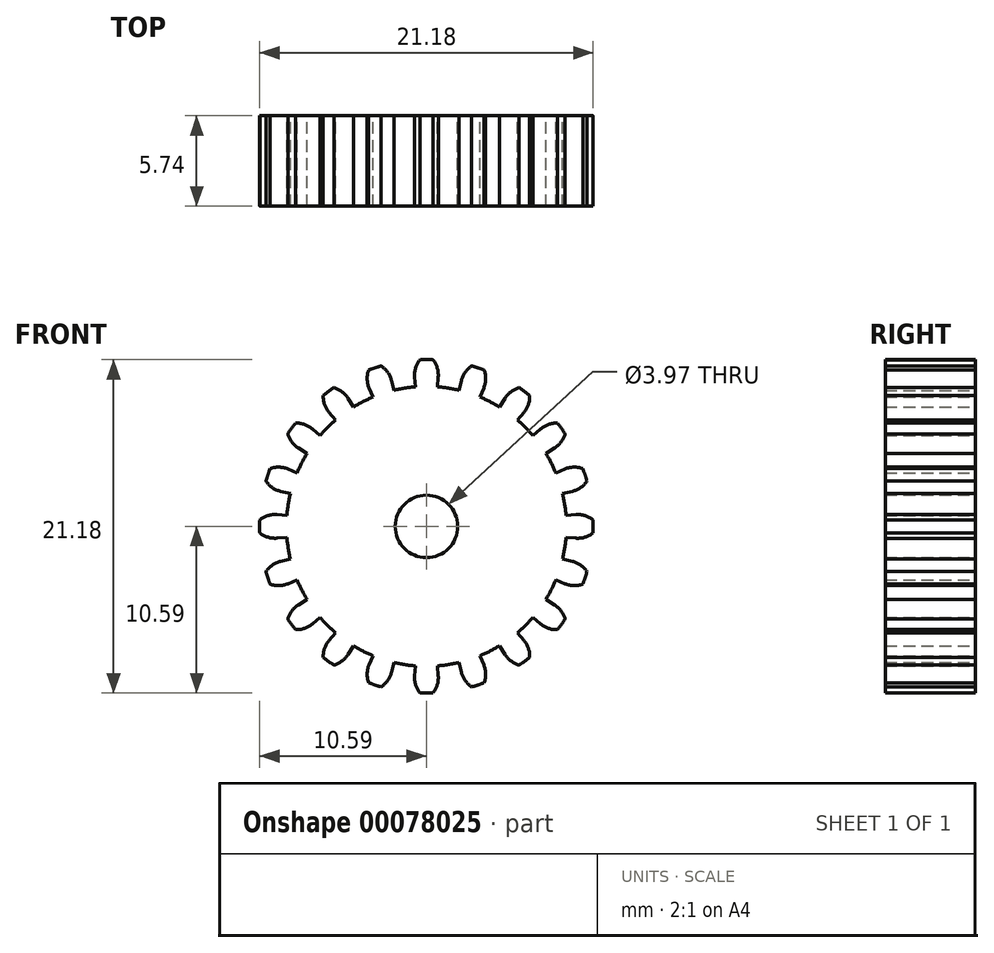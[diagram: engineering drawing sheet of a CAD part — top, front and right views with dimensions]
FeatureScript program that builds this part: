
annotation { "Feature Type Name" : "Feature", "Feature Type Description" : "" }
export const myFeature = defineFeature(function(context is Context, id is Id, definition is map)
    precondition{}
    {
        {
            var Q0;
            Q0=qCreatedBy(makeId("Front.planeOp"),FACE);
            var sketch = newSketch(context, id + "F0", { "sketchPlane" : qUnion([Q0])});
            skCircle(sketch, "E0", {"center": v(0, 0) * mm, "radius": 10.6 * mm, "construction": true});
            skCircle(sketch, "E1", {"center": v(0, 0) * mm, "radius": 9.53 * mm, "construction": true});
            skCircle(sketch, "E2", {"center": v(0, 0) * mm, "radius": 8.9 * mm, "construction": true});
            skLineSegment(sketch, "E3", {"start": v(0, 0) * mm, "end": v(8.78, 1.4) * mm, "construction": true});
            skLineSegment(sketch, "E4", {"start": v(0, 0) * mm, "end": v(6.61, 0) * mm, "construction": true});
            skLineSegment(sketch, "E5", {"start": v(0, 0) * mm, "end": v(6.84, 0.54) * mm, "construction": true});
            skLineSegment(sketch, "E6", {"start": v(0, 0) * mm, "end": v(7.15, 0.28) * mm, "construction": true});
            skArc(sketch, "E7", {"start": v(10.58, 0.42) * mm, "mid": v(10.59, 0.2) * mm, "end": v(10.6, 0) * mm});
            skArc(sketch, "E8", {"start": v(8.78, 1.4) * mm, "mid": v(8.83, 1.04) * mm, "end": v(8.86, 0.7) * mm});
            skLineSegment(sketch, "E9", {"start": v(8.86, 0.7) * mm, "end": v(9.5, 0.75) * mm});
            skArc(sketch, "E10", {"start": v(9.5, 0.75) * mm, "mid": v(10.07, 0.68) * mm, "end": v(10.58, 0.42) * mm});
            skLineSegment(sketch, "E11", {"start": v(0, 0) * mm, "end": v(8.78, 1.4) * mm});
            skLineSegment(sketch, "E12", {"start": v(0, 0) * mm, "end": v(10.6, 0) * mm});
            skArc(sketch, "E13.MirrorCS", {"start": v(8.78, -1.4) * mm, "mid": v(8.83, -1.04) * mm, "end": v(8.86, -0.7) * mm});
            skLineSegment(sketch, "E14.MirrorCS", {"start": v(8.86, -0.7) * mm, "end": v(9.5, -0.75) * mm});
            skArc(sketch, "E15.MirrorCS", {"start": v(9.5, -0.75) * mm, "mid": v(10.07, -0.68) * mm, "end": v(10.58, -0.42) * mm});
            skArc(sketch, "E16.MirrorCS", {"start": v(10.58, -0.42) * mm, "mid": v(10.59, -0.2) * mm, "end": v(10.6, 0) * mm});
            skArc(sketch, "E17.1.0", {"start": v(7.92, 4.04) * mm, "mid": v(8.07, 3.72) * mm, "end": v(8.21, 3.4) * mm});
            skLineSegment(sketch, "E17.1.1", {"start": v(8.21, 3.4) * mm, "end": v(8.8, 3.65) * mm});
            skArc(sketch, "E17.1.2", {"start": v(8.8, 3.65) * mm, "mid": v(9.37, 3.76) * mm, "end": v(9.94, 3.67) * mm});
            skArc(sketch, "E17.1.3", {"start": v(9.94, 3.67) * mm, "mid": v(10, 3.47) * mm, "end": v(10.07, 3.27) * mm});
            skArc(sketch, "E17.1.4", {"start": v(10.2, 2.88) * mm, "mid": v(10.14, 3.07) * mm, "end": v(10.07, 3.27) * mm});
            skArc(sketch, "E17.1.5", {"start": v(9.26, 2.22) * mm, "mid": v(9.79, 2.46) * mm, "end": v(10.2, 2.88) * mm});
            skLineSegment(sketch, "E17.1.6", {"start": v(8.64, 2.08) * mm, "end": v(9.26, 2.22) * mm});
            skArc(sketch, "E17.1.7", {"start": v(8.78, 1.4) * mm, "mid": v(8.72, 1.73) * mm, "end": v(8.64, 2.08) * mm});
            skArc(sketch, "E17.2.0", {"start": v(6.29, 6.29) * mm, "mid": v(6.53, 6.03) * mm, "end": v(6.76, 5.77) * mm});
            skLineSegment(sketch, "E17.2.1", {"start": v(6.76, 5.77) * mm, "end": v(7.24, 6.19) * mm});
            skArc(sketch, "E17.2.2", {"start": v(7.24, 6.19) * mm, "mid": v(7.75, 6.47) * mm, "end": v(8.32, 6.56) * mm});
            skArc(sketch, "E17.2.3", {"start": v(8.32, 6.56) * mm, "mid": v(8.45, 6.4) * mm, "end": v(8.57, 6.23) * mm});
            skArc(sketch, "E17.2.4", {"start": v(8.8, 5.88) * mm, "mid": v(8.69, 6.06) * mm, "end": v(8.57, 6.23) * mm});
            skArc(sketch, "E17.2.5", {"start": v(8.12, 4.98) * mm, "mid": v(8.55, 5.37) * mm, "end": v(8.8, 5.88) * mm});
            skLineSegment(sketch, "E17.2.6", {"start": v(7.58, 4.65) * mm, "end": v(8.12, 4.98) * mm});
            skArc(sketch, "E17.2.7", {"start": v(7.92, 4.04) * mm, "mid": v(7.76, 4.34) * mm, "end": v(7.58, 4.65) * mm});
            skArc(sketch, "E17.3.0", {"start": v(4.04, 7.92) * mm, "mid": v(4.34, 7.76) * mm, "end": v(4.65, 7.58) * mm});
            skLineSegment(sketch, "E17.3.1", {"start": v(4.65, 7.58) * mm, "end": v(4.98, 8.12) * mm});
            skArc(sketch, "E17.3.2", {"start": v(4.98, 8.12) * mm, "mid": v(5.37, 8.55) * mm, "end": v(5.88, 8.8) * mm});
            skArc(sketch, "E17.3.3", {"start": v(5.88, 8.8) * mm, "mid": v(6.06, 8.69) * mm, "end": v(6.23, 8.57) * mm});
            skArc(sketch, "E17.3.4", {"start": v(6.56, 8.32) * mm, "mid": v(6.4, 8.45) * mm, "end": v(6.23, 8.57) * mm});
            skArc(sketch, "E17.3.5", {"start": v(6.19, 7.24) * mm, "mid": v(6.47, 7.75) * mm, "end": v(6.56, 8.32) * mm});
            skLineSegment(sketch, "E17.3.6", {"start": v(5.77, 6.76) * mm, "end": v(6.19, 7.24) * mm});
            skArc(sketch, "E17.3.7", {"start": v(6.29, 6.29) * mm, "mid": v(6.03, 6.53) * mm, "end": v(5.77, 6.76) * mm});
            skArc(sketch, "E17.4.0", {"start": v(1.4, 8.78) * mm, "mid": v(1.73, 8.72) * mm, "end": v(2.08, 8.64) * mm});
            skLineSegment(sketch, "E17.4.1", {"start": v(2.08, 8.64) * mm, "end": v(2.22, 9.26) * mm});
            skArc(sketch, "E17.4.2", {"start": v(2.22, 9.26) * mm, "mid": v(2.46, 9.79) * mm, "end": v(2.88, 10.2) * mm});
            skArc(sketch, "E17.4.3", {"start": v(2.88, 10.2) * mm, "mid": v(3.07, 10.14) * mm, "end": v(3.27, 10.07) * mm});
            skArc(sketch, "E17.4.4", {"start": v(3.67, 9.94) * mm, "mid": v(3.47, 10) * mm, "end": v(3.27, 10.07) * mm});
            skArc(sketch, "E17.4.5", {"start": v(3.65, 8.8) * mm, "mid": v(3.76, 9.37) * mm, "end": v(3.67, 9.94) * mm});
            skLineSegment(sketch, "E17.4.6", {"start": v(3.4, 8.21) * mm, "end": v(3.65, 8.8) * mm});
            skArc(sketch, "E17.4.7", {"start": v(4.04, 7.92) * mm, "mid": v(3.72, 8.07) * mm, "end": v(3.4, 8.21) * mm});
            skArc(sketch, "E17.5.0", {"start": v(-1.4, 8.78) * mm, "mid": v(-1.04, 8.83) * mm, "end": v(-0.7, 8.86) * mm});
            skLineSegment(sketch, "E17.5.1", {"start": v(-0.7, 8.86) * mm, "end": v(-0.75, 9.5) * mm});
            skArc(sketch, "E17.5.2", {"start": v(-0.75, 9.5) * mm, "mid": v(-0.68, 10.07) * mm, "end": v(-0.42, 10.58) * mm});
            skArc(sketch, "E17.5.3", {"start": v(-0.42, 10.58) * mm, "mid": v(-0.2, 10.59) * mm, "end": v(0, 10.6) * mm});
            skArc(sketch, "E17.5.4", {"start": v(0.42, 10.58) * mm, "mid": v(0.2, 10.59) * mm, "end": v(0, 10.6) * mm});
            skArc(sketch, "E17.5.5", {"start": v(0.75, 9.5) * mm, "mid": v(0.68, 10.07) * mm, "end": v(0.42, 10.58) * mm});
            skLineSegment(sketch, "E17.5.6", {"start": v(0.7, 8.86) * mm, "end": v(0.75, 9.5) * mm});
            skArc(sketch, "E17.5.7", {"start": v(1.4, 8.78) * mm, "mid": v(1.04, 8.83) * mm, "end": v(0.7, 8.86) * mm});
            skArc(sketch, "E17.6.0", {"start": v(-4.04, 7.92) * mm, "mid": v(-3.72, 8.07) * mm, "end": v(-3.4, 8.21) * mm});
            skLineSegment(sketch, "E17.6.1", {"start": v(-3.4, 8.21) * mm, "end": v(-3.65, 8.8) * mm});
            skArc(sketch, "E17.6.2", {"start": v(-3.65, 8.8) * mm, "mid": v(-3.76, 9.37) * mm, "end": v(-3.67, 9.94) * mm});
            skArc(sketch, "E17.6.3", {"start": v(-3.67, 9.94) * mm, "mid": v(-3.47, 10) * mm, "end": v(-3.27, 10.07) * mm});
            skArc(sketch, "E17.6.4", {"start": v(-2.88, 10.2) * mm, "mid": v(-3.07, 10.14) * mm, "end": v(-3.27, 10.07) * mm});
            skArc(sketch, "E17.6.5", {"start": v(-2.22, 9.26) * mm, "mid": v(-2.46, 9.79) * mm, "end": v(-2.88, 10.2) * mm});
            skLineSegment(sketch, "E17.6.6", {"start": v(-2.08, 8.64) * mm, "end": v(-2.22, 9.26) * mm});
            skArc(sketch, "E17.6.7", {"start": v(-1.4, 8.78) * mm, "mid": v(-1.73, 8.72) * mm, "end": v(-2.08, 8.64) * mm});
            skArc(sketch, "E17.7.0", {"start": v(-6.29, 6.29) * mm, "mid": v(-6.03, 6.53) * mm, "end": v(-5.77, 6.76) * mm});
            skLineSegment(sketch, "E17.7.1", {"start": v(-5.77, 6.76) * mm, "end": v(-6.19, 7.24) * mm});
            skArc(sketch, "E17.7.2", {"start": v(-6.19, 7.24) * mm, "mid": v(-6.47, 7.75) * mm, "end": v(-6.56, 8.32) * mm});
            skArc(sketch, "E17.7.3", {"start": v(-6.56, 8.32) * mm, "mid": v(-6.4, 8.45) * mm, "end": v(-6.23, 8.57) * mm});
            skArc(sketch, "E17.7.4", {"start": v(-5.88, 8.8) * mm, "mid": v(-6.06, 8.69) * mm, "end": v(-6.23, 8.57) * mm});
            skArc(sketch, "E17.7.5", {"start": v(-4.98, 8.12) * mm, "mid": v(-5.37, 8.55) * mm, "end": v(-5.88, 8.8) * mm});
            skLineSegment(sketch, "E17.7.6", {"start": v(-4.65, 7.58) * mm, "end": v(-4.98, 8.12) * mm});
            skArc(sketch, "E17.7.7", {"start": v(-4.04, 7.92) * mm, "mid": v(-4.34, 7.76) * mm, "end": v(-4.65, 7.58) * mm});
            skArc(sketch, "E17.8.0", {"start": v(-7.92, 4.04) * mm, "mid": v(-7.76, 4.34) * mm, "end": v(-7.58, 4.65) * mm});
            skLineSegment(sketch, "E17.8.1", {"start": v(-7.58, 4.65) * mm, "end": v(-8.12, 4.98) * mm});
            skArc(sketch, "E17.8.2", {"start": v(-8.12, 4.98) * mm, "mid": v(-8.55, 5.37) * mm, "end": v(-8.8, 5.88) * mm});
            skArc(sketch, "E17.8.3", {"start": v(-8.8, 5.88) * mm, "mid": v(-8.69, 6.06) * mm, "end": v(-8.57, 6.23) * mm});
            skArc(sketch, "E17.8.4", {"start": v(-8.32, 6.56) * mm, "mid": v(-8.45, 6.4) * mm, "end": v(-8.57, 6.23) * mm});
            skArc(sketch, "E17.8.5", {"start": v(-7.24, 6.19) * mm, "mid": v(-7.75, 6.47) * mm, "end": v(-8.32, 6.56) * mm});
            skLineSegment(sketch, "E17.8.6", {"start": v(-6.76, 5.77) * mm, "end": v(-7.24, 6.19) * mm});
            skArc(sketch, "E17.8.7", {"start": v(-6.29, 6.29) * mm, "mid": v(-6.53, 6.03) * mm, "end": v(-6.76, 5.77) * mm});
            skArc(sketch, "E17.9.0", {"start": v(-8.78, 1.4) * mm, "mid": v(-8.72, 1.73) * mm, "end": v(-8.64, 2.08) * mm});
            skLineSegment(sketch, "E17.9.1", {"start": v(-8.64, 2.08) * mm, "end": v(-9.26, 2.22) * mm});
            skArc(sketch, "E17.9.2", {"start": v(-9.26, 2.22) * mm, "mid": v(-9.79, 2.46) * mm, "end": v(-10.2, 2.88) * mm});
            skArc(sketch, "E17.9.3", {"start": v(-10.2, 2.88) * mm, "mid": v(-10.14, 3.07) * mm, "end": v(-10.07, 3.27) * mm});
            skArc(sketch, "E17.9.4", {"start": v(-9.94, 3.67) * mm, "mid": v(-10, 3.47) * mm, "end": v(-10.07, 3.27) * mm});
            skArc(sketch, "E17.9.5", {"start": v(-8.8, 3.65) * mm, "mid": v(-9.37, 3.76) * mm, "end": v(-9.94, 3.67) * mm});
            skLineSegment(sketch, "E17.9.6", {"start": v(-8.21, 3.4) * mm, "end": v(-8.8, 3.65) * mm});
            skArc(sketch, "E17.9.7", {"start": v(-7.92, 4.04) * mm, "mid": v(-8.07, 3.72) * mm, "end": v(-8.21, 3.4) * mm});
            skCircle(sketch, "E18", {"center": v(0, 0) * mm, "radius": 1.98 * mm});
            skArc(sketch, "E19.1.10.0", {"start": v(-8.78, -1.4) * mm, "mid": v(-8.83, -1.04) * mm, "end": v(-8.86, -0.7) * mm});
            skLineSegment(sketch, "E19.4.10.0", {"start": v(-8.86, -0.7) * mm, "end": v(-9.5, -0.75) * mm});
            skArc(sketch, "E19.7.10.0", {"start": v(-9.5, -0.75) * mm, "mid": v(-10.07, -0.68) * mm, "end": v(-10.58, -0.42) * mm});
            skArc(sketch, "E19.11.10.0", {"start": v(-10.58, -0.42) * mm, "mid": v(-10.59, -0.2) * mm, "end": v(-10.6, 0) * mm});
            skArc(sketch, "E19.15.10.0", {"start": v(-10.58, 0.42) * mm, "mid": v(-10.59, 0.2) * mm, "end": v(-10.6, 0) * mm});
            skArc(sketch, "E19.19.10.0", {"start": v(-9.5, 0.75) * mm, "mid": v(-10.07, 0.68) * mm, "end": v(-10.58, 0.42) * mm});
            skLineSegment(sketch, "E19.23.10.0", {"start": v(-8.86, 0.7) * mm, "end": v(-9.5, 0.75) * mm});
            skArc(sketch, "E19.26.10.0", {"start": v(-8.78, 1.4) * mm, "mid": v(-8.83, 1.04) * mm, "end": v(-8.86, 0.7) * mm});
            skArc(sketch, "E19.1.11.0", {"start": v(-7.92, -4.04) * mm, "mid": v(-8.07, -3.72) * mm, "end": v(-8.21, -3.4) * mm});
            skLineSegment(sketch, "E19.4.11.0", {"start": v(-8.21, -3.4) * mm, "end": v(-8.8, -3.65) * mm});
            skArc(sketch, "E19.7.11.0", {"start": v(-8.8, -3.65) * mm, "mid": v(-9.37, -3.76) * mm, "end": v(-9.94, -3.67) * mm});
            skArc(sketch, "E19.11.11.0", {"start": v(-9.94, -3.67) * mm, "mid": v(-10, -3.47) * mm, "end": v(-10.07, -3.27) * mm});
            skArc(sketch, "E19.15.11.0", {"start": v(-10.2, -2.88) * mm, "mid": v(-10.14, -3.07) * mm, "end": v(-10.07, -3.27) * mm});
            skArc(sketch, "E19.19.11.0", {"start": v(-9.26, -2.22) * mm, "mid": v(-9.79, -2.46) * mm, "end": v(-10.2, -2.88) * mm});
            skLineSegment(sketch, "E19.23.11.0", {"start": v(-8.64, -2.08) * mm, "end": v(-9.26, -2.22) * mm});
            skArc(sketch, "E19.26.11.0", {"start": v(-8.78, -1.4) * mm, "mid": v(-8.72, -1.73) * mm, "end": v(-8.64, -2.08) * mm});
            skArc(sketch, "E19.1.12.0", {"start": v(-6.29, -6.29) * mm, "mid": v(-6.53, -6.03) * mm, "end": v(-6.76, -5.77) * mm});
            skLineSegment(sketch, "E19.4.12.0", {"start": v(-6.76, -5.77) * mm, "end": v(-7.24, -6.19) * mm});
            skArc(sketch, "E19.7.12.0", {"start": v(-7.24, -6.19) * mm, "mid": v(-7.75, -6.47) * mm, "end": v(-8.32, -6.56) * mm});
            skArc(sketch, "E19.11.12.0", {"start": v(-8.32, -6.56) * mm, "mid": v(-8.45, -6.4) * mm, "end": v(-8.57, -6.23) * mm});
            skArc(sketch, "E19.15.12.0", {"start": v(-8.8, -5.88) * mm, "mid": v(-8.69, -6.06) * mm, "end": v(-8.57, -6.23) * mm});
            skArc(sketch, "E19.19.12.0", {"start": v(-8.12, -4.98) * mm, "mid": v(-8.55, -5.37) * mm, "end": v(-8.8, -5.88) * mm});
            skLineSegment(sketch, "E19.23.12.0", {"start": v(-7.58, -4.65) * mm, "end": v(-8.12, -4.98) * mm});
            skArc(sketch, "E19.26.12.0", {"start": v(-7.92, -4.04) * mm, "mid": v(-7.76, -4.34) * mm, "end": v(-7.58, -4.65) * mm});
            skArc(sketch, "E19.1.13.0", {"start": v(-4.04, -7.92) * mm, "mid": v(-4.34, -7.76) * mm, "end": v(-4.65, -7.58) * mm});
            skLineSegment(sketch, "E19.4.13.0", {"start": v(-4.65, -7.58) * mm, "end": v(-4.98, -8.12) * mm});
            skArc(sketch, "E19.7.13.0", {"start": v(-4.98, -8.12) * mm, "mid": v(-5.37, -8.55) * mm, "end": v(-5.88, -8.8) * mm});
            skArc(sketch, "E19.11.13.0", {"start": v(-5.88, -8.8) * mm, "mid": v(-6.06, -8.69) * mm, "end": v(-6.23, -8.57) * mm});
            skArc(sketch, "E19.15.13.0", {"start": v(-6.56, -8.32) * mm, "mid": v(-6.4, -8.45) * mm, "end": v(-6.23, -8.57) * mm});
            skArc(sketch, "E19.19.13.0", {"start": v(-6.19, -7.24) * mm, "mid": v(-6.47, -7.75) * mm, "end": v(-6.56, -8.32) * mm});
            skLineSegment(sketch, "E19.23.13.0", {"start": v(-5.77, -6.76) * mm, "end": v(-6.19, -7.24) * mm});
            skArc(sketch, "E19.26.13.0", {"start": v(-6.29, -6.29) * mm, "mid": v(-6.03, -6.53) * mm, "end": v(-5.77, -6.76) * mm});
            skArc(sketch, "E19.1.14.0", {"start": v(-1.4, -8.78) * mm, "mid": v(-1.73, -8.72) * mm, "end": v(-2.08, -8.64) * mm});
            skLineSegment(sketch, "E19.4.14.0", {"start": v(-2.08, -8.64) * mm, "end": v(-2.22, -9.26) * mm});
            skArc(sketch, "E19.7.14.0", {"start": v(-2.22, -9.26) * mm, "mid": v(-2.46, -9.79) * mm, "end": v(-2.88, -10.2) * mm});
            skArc(sketch, "E19.11.14.0", {"start": v(-2.88, -10.2) * mm, "mid": v(-3.07, -10.14) * mm, "end": v(-3.27, -10.07) * mm});
            skArc(sketch, "E19.15.14.0", {"start": v(-3.67, -9.94) * mm, "mid": v(-3.47, -10) * mm, "end": v(-3.27, -10.07) * mm});
            skArc(sketch, "E19.19.14.0", {"start": v(-3.65, -8.8) * mm, "mid": v(-3.76, -9.37) * mm, "end": v(-3.67, -9.94) * mm});
            skLineSegment(sketch, "E19.23.14.0", {"start": v(-3.4, -8.21) * mm, "end": v(-3.65, -8.8) * mm});
            skArc(sketch, "E19.26.14.0", {"start": v(-4.04, -7.92) * mm, "mid": v(-3.72, -8.07) * mm, "end": v(-3.4, -8.21) * mm});
            skArc(sketch, "E19.1.15.0", {"start": v(1.4, -8.78) * mm, "mid": v(1.04, -8.83) * mm, "end": v(0.7, -8.86) * mm});
            skLineSegment(sketch, "E19.4.15.0", {"start": v(0.7, -8.86) * mm, "end": v(0.75, -9.5) * mm});
            skArc(sketch, "E19.7.15.0", {"start": v(0.75, -9.5) * mm, "mid": v(0.68, -10.07) * mm, "end": v(0.42, -10.58) * mm});
            skArc(sketch, "E19.11.15.0", {"start": v(0.42, -10.58) * mm, "mid": v(0.2, -10.59) * mm, "end": v(0, -10.6) * mm});
            skArc(sketch, "E19.15.15.0", {"start": v(-0.42, -10.58) * mm, "mid": v(-0.2, -10.59) * mm, "end": v(0, -10.6) * mm});
            skArc(sketch, "E19.19.15.0", {"start": v(-0.75, -9.5) * mm, "mid": v(-0.68, -10.07) * mm, "end": v(-0.42, -10.58) * mm});
            skLineSegment(sketch, "E19.23.15.0", {"start": v(-0.7, -8.86) * mm, "end": v(-0.75, -9.5) * mm});
            skArc(sketch, "E19.26.15.0", {"start": v(-1.4, -8.78) * mm, "mid": v(-1.04, -8.83) * mm, "end": v(-0.7, -8.86) * mm});
            skArc(sketch, "E19.1.16.0", {"start": v(4.04, -7.92) * mm, "mid": v(3.72, -8.07) * mm, "end": v(3.4, -8.21) * mm});
            skLineSegment(sketch, "E19.4.16.0", {"start": v(3.4, -8.21) * mm, "end": v(3.65, -8.8) * mm});
            skArc(sketch, "E19.7.16.0", {"start": v(3.65, -8.8) * mm, "mid": v(3.76, -9.37) * mm, "end": v(3.67, -9.94) * mm});
            skArc(sketch, "E19.11.16.0", {"start": v(3.67, -9.94) * mm, "mid": v(3.47, -10) * mm, "end": v(3.27, -10.07) * mm});
            skArc(sketch, "E19.15.16.0", {"start": v(2.88, -10.2) * mm, "mid": v(3.07, -10.14) * mm, "end": v(3.27, -10.07) * mm});
            skArc(sketch, "E19.19.16.0", {"start": v(2.22, -9.26) * mm, "mid": v(2.46, -9.79) * mm, "end": v(2.88, -10.2) * mm});
            skLineSegment(sketch, "E19.23.16.0", {"start": v(2.08, -8.64) * mm, "end": v(2.22, -9.26) * mm});
            skArc(sketch, "E19.26.16.0", {"start": v(1.4, -8.78) * mm, "mid": v(1.73, -8.72) * mm, "end": v(2.08, -8.64) * mm});
            skArc(sketch, "E19.1.17.0", {"start": v(6.29, -6.29) * mm, "mid": v(6.03, -6.53) * mm, "end": v(5.77, -6.76) * mm});
            skLineSegment(sketch, "E19.4.17.0", {"start": v(5.77, -6.76) * mm, "end": v(6.19, -7.24) * mm});
            skArc(sketch, "E19.7.17.0", {"start": v(6.19, -7.24) * mm, "mid": v(6.47, -7.75) * mm, "end": v(6.56, -8.32) * mm});
            skArc(sketch, "E19.11.17.0", {"start": v(6.56, -8.32) * mm, "mid": v(6.4, -8.45) * mm, "end": v(6.23, -8.57) * mm});
            skArc(sketch, "E19.15.17.0", {"start": v(5.88, -8.8) * mm, "mid": v(6.06, -8.69) * mm, "end": v(6.23, -8.57) * mm});
            skArc(sketch, "E19.19.17.0", {"start": v(4.98, -8.12) * mm, "mid": v(5.37, -8.55) * mm, "end": v(5.88, -8.8) * mm});
            skLineSegment(sketch, "E19.23.17.0", {"start": v(4.65, -7.58) * mm, "end": v(4.98, -8.12) * mm});
            skArc(sketch, "E19.26.17.0", {"start": v(4.04, -7.92) * mm, "mid": v(4.34, -7.76) * mm, "end": v(4.65, -7.58) * mm});
            skArc(sketch, "E19.1.18.0", {"start": v(7.92, -4.04) * mm, "mid": v(7.76, -4.34) * mm, "end": v(7.58, -4.65) * mm});
            skLineSegment(sketch, "E19.4.18.0", {"start": v(7.58, -4.65) * mm, "end": v(8.12, -4.98) * mm});
            skArc(sketch, "E19.7.18.0", {"start": v(8.12, -4.98) * mm, "mid": v(8.55, -5.37) * mm, "end": v(8.8, -5.88) * mm});
            skArc(sketch, "E19.11.18.0", {"start": v(8.8, -5.88) * mm, "mid": v(8.69, -6.06) * mm, "end": v(8.57, -6.23) * mm});
            skArc(sketch, "E19.15.18.0", {"start": v(8.32, -6.56) * mm, "mid": v(8.45, -6.4) * mm, "end": v(8.57, -6.23) * mm});
            skArc(sketch, "E19.19.18.0", {"start": v(7.24, -6.19) * mm, "mid": v(7.75, -6.47) * mm, "end": v(8.32, -6.56) * mm});
            skLineSegment(sketch, "E19.23.18.0", {"start": v(6.76, -5.77) * mm, "end": v(7.24, -6.19) * mm});
            skArc(sketch, "E19.26.18.0", {"start": v(6.29, -6.29) * mm, "mid": v(6.53, -6.03) * mm, "end": v(6.76, -5.77) * mm});
            skArc(sketch, "E19.1.19.0", {"start": v(8.78, -1.4) * mm, "mid": v(8.72, -1.73) * mm, "end": v(8.64, -2.08) * mm});
            skLineSegment(sketch, "E19.4.19.0", {"start": v(8.64, -2.08) * mm, "end": v(9.26, -2.22) * mm});
            skArc(sketch, "E19.7.19.0", {"start": v(9.26, -2.22) * mm, "mid": v(9.79, -2.46) * mm, "end": v(10.2, -2.88) * mm});
            skArc(sketch, "E19.11.19.0", {"start": v(10.2, -2.88) * mm, "mid": v(10.14, -3.07) * mm, "end": v(10.07, -3.27) * mm});
            skArc(sketch, "E19.15.19.0", {"start": v(9.94, -3.67) * mm, "mid": v(10, -3.47) * mm, "end": v(10.07, -3.27) * mm});
            skArc(sketch, "E19.19.19.0", {"start": v(8.8, -3.65) * mm, "mid": v(9.37, -3.76) * mm, "end": v(9.94, -3.67) * mm});
            skLineSegment(sketch, "E19.23.19.0", {"start": v(8.21, -3.4) * mm, "end": v(8.8, -3.65) * mm});
            skArc(sketch, "E19.26.19.0", {"start": v(7.92, -4.04) * mm, "mid": v(8.07, -3.72) * mm, "end": v(8.21, -3.4) * mm});
            skSolve(sketch);
        }
        {
            var Q0;
            Q0 = qSketchRegion(id + "F0", true);
            extrude(context, id + "F1", {"entities" : qUnion([Q0]), "endBound" : BoundingType.SYMMETRIC, "depth" : 5.74 * mm});
        }
    });
